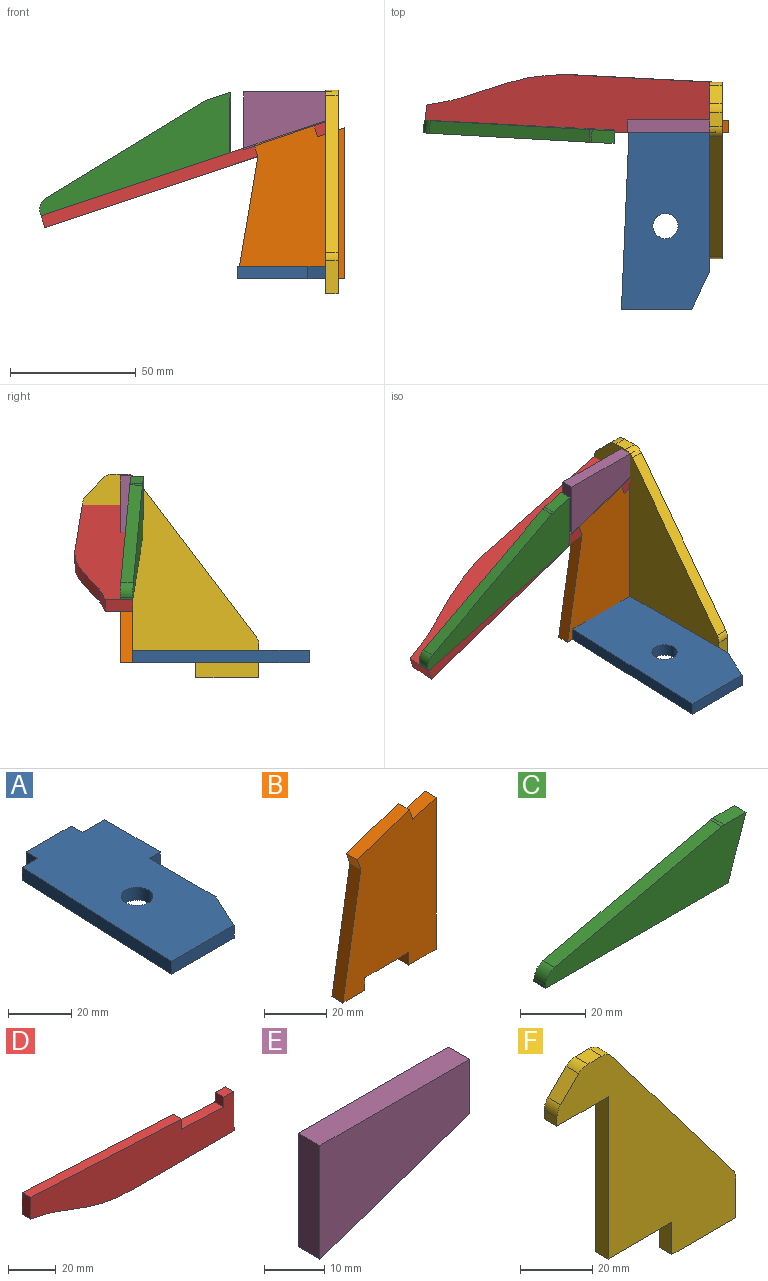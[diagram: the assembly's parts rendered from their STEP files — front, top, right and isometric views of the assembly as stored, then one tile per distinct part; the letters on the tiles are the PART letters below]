
ASSEMBLY  parts=6 mates=5
PART A: 14 faces, bbox 40x75x5 mm
  f0: plane 75x40mm, normal (0,0,1), area 2439mm2, adj f2,f3,f4,f5,f6,f7,f8,f9
  f1: plane 75x40mm, normal (0,0,-1), area 2439mm2, adj f2,f3,f4,f5,f6,f7,f8,f9
  f2: plane 10x5mm, normal (0,1,0), area 50mm2, adj f0,f1,f3,f11
  f3: plane 5x5mm, normal (1,0,0), area 25mm2, adj f0,f1,f2,f4
  f4: plane 20x5mm, normal (0,1,0), area 100mm2, adj f0,f1,f3,f5
  f5: plane 5x5mm, normal (-1,0,0), area 25mm2, adj f0,f1,f4,f6
  f6: plane 7x5mm, normal (0,1,0), area 35mm2, adj f0,f1,f5,f7
  f7: plane 70x5mm, normal (-1,0.04,0), area 350.3mm2, adj f0,f1,f6,f8
  f8: plane 28x5mm, normal (0,-1,0), area 140mm2, adj f0,f1,f7,f13
  f9: plane 30x5mm, normal (1,0,0), area 150mm2, adj f0,f1,f10,f13
  f10: plane 5x5mm, normal (0,-1,0), area 25mm2, adj f0,f1,f9,f11
  f11: plane 25x5mm, normal (1,0,0), area 125mm2, adj f0,f1,f2,f10
  f12: cylinder r=5mm len=10mm, axis (0,0,-1), area 157.1mm2, adj f0,f1
  f13: plane 15x7mm, normal (0.91,-0.42,0), area 82.8mm2, adj f0,f1,f8,f9
PART B: 13 faces, bbox 42.5x5x61.2 mm
  f0: plane 10x5mm, normal (0,0,-1), area 50mm2, adj f1,f10,f11,f12
  f1: plane 5x5mm, normal (1,0,0), area 25mm2, adj f0,f2,f11,f12
  f2: plane 20x5mm, normal (0,0,-1), area 100mm2, adj f1,f3,f11,f12
  f3: plane 5x5mm, normal (-1,0,0), area 25mm2, adj f2,f4,f11,f12
  f4: plane 12.5x5mm, normal (0,0,-1), area 62.5mm2, adj f3,f5,f11,f12
  f5: plane 60x5mm, normal (1,0,0), area 300mm2, adj f4,f6,f11,f12
  f6: plane 10.64x5mm, normal (-0.32,0,0.95), area 56.1mm2, adj f5,f7,f11,f12
  f7: plane 5x4.74mm, normal (0.95,0,0.32), area 25mm2, adj f6,f8,f11,f12
  f8: plane 23.72x7.91mm, normal (-0.32,0,0.95), area 125mm2, adj f7,f9,f11,f12
  f9: plane 5x4.74mm, normal (-0.95,0,-0.32), area 25mm2, adj f8,f10,f11,f12
  f10: plane 48.55x8.14mm, normal (-0.99,0,0.17), area 246.1mm2, adj f0,f9,f11,f12
  f11: plane 61.2x42.5mm, normal (0,-1,0), area 2087.4mm2, adj f0,f1,f2,f3,f4,f5,f6,f7
  f12: plane 61.2x42.5mm, normal (0,1,0), area 2087.4mm2, adj f0,f1,f2,f3,f4,f5,f6,f7
PART C: 9 faces, bbox 86.8x5x22.7 mm
  f0: cylinder r=5mm len=5mm, axis (0,1,0), area 33.6mm2, adj f1,f6,f7,f8
  f1: plane 5x1.02mm, normal (-1,0,0), area 5.1mm2, adj f0,f2,f7,f8
  f2: plane 79x5mm, normal (0,0,-1), area 395mm2, adj f1,f3,f7,f8
  f3: plane 22.69x7.81mm, normal (0.95,0,-0.33), area 120mm2, adj f2,f4,f7,f8
  f4: plane 9.43x5mm, normal (0,0,1), area 47.2mm2, adj f3,f5,f7,f8
  f5: cylinder r=5mm len=5mm, axis (0,1,0), area 5.7mm2, adj f4,f6,f7,f8
  f6: plane 72.38x16.67mm, normal (-0.22,0,0.97), area 371.4mm2, adj f0,f5,f7,f8
  f7: plane 86.81x22.69mm, normal (0,-1,0), area 1198.7mm2, adj f0,f1,f2,f3,f4,f5,f6
  f8: plane 86.81x22.69mm, normal (0,1,0), area 1198.7mm2, adj f0,f1,f2,f3,f4,f5,f6
PART D: 14 faces, bbox 120x5x26 mm
  f0: plane 5.99x5mm, normal (0.05,0,1), area 30mm2, adj f1,f2,f3,f11
  f1: plane 120x26mm, normal (0,-1,0), area 2251.6mm2, adj f0,f3,f4,f5,f6,f7,f8,f9
  f2: plane 120x26mm, normal (0,1,0), area 2251.6mm2, adj f0,f3,f4,f5,f6,f7,f8,f9
  f3: plane 20x5mm, normal (1,0,0), area 100mm2, adj f0,f1,f2,f10
  f4: plane 89.04x5mm, normal (0.05,0,1), area 445.7mm2, adj f1,f2,f5,f12
  f5: plane 11x5mm, normal (-1,0,0), area 55mm2, adj f1,f2,f4,f6
  f6: plane 9.75x5mm, normal (-0.22,0,-0.97), area 50mm2, adj f1,f2,f5,f7
  f7: cylinder r=40mm len=5mm, axis (0,1,0), area 24.4mm2, adj f1,f2,f6,f8
  f8: plane 18.4x6.64mm, normal (-0.34,0,-0.94), area 97.8mm2, adj f1,f2,f7,f9
  f9: cylinder r=80mm len=27.17mm, axis (0,1,0), area 138.6mm2, adj f1,f2,f8,f10
  f10: plane 60x5mm, normal (0,0,-1), area 300mm2, adj f1,f2,f3,f9
  f11: plane 5x4.99mm, normal (-1,0,0.05), area 25mm2, adj f0,f1,f2,f13
  f12: plane 5x4.99mm, normal (1,0,-0.05), area 25mm2, adj f1,f2,f4,f13
  f13: plane 24.97x5mm, normal (0.05,0,1), area 125mm2, adj f1,f2,f11,f12
PART E: 6 faces, bbox 35x5x23 mm
  f0: plane 35x5mm, normal (0,0,1), area 175mm2, adj f1,f3,f4,f5
  f1: plane 23x5mm, normal (-1,0,0), area 115mm2, adj f0,f2,f4,f5
  f2: plane 35x12mm, normal (0.32,0,-0.95), area 185mm2, adj f1,f3,f4,f5
  f3: plane 11x5mm, normal (1,0,0), area 55mm2, adj f0,f2,f4,f5
  f4: plane 35x23mm, normal (0,-1,0), area 595mm2, adj f0,f1,f2,f3
  f5: plane 35x23mm, normal (0,1,0), area 595mm2, adj f0,f1,f2,f3
PART F: 16 faces, bbox 70x5x81 mm
  f0: plane 13.32x5mm, normal (1,0,0), area 66.6mm2, adj f9,f10,f11,f12
  f1: plane 62.68x47.49mm, normal (0.8,0,0.6), area 393.2mm2, adj f10,f11,f12,f13
  f2: plane 5.44x5mm, normal (0,0,1), area 27.2mm2, adj f10,f11,f13,f14
  f3: plane 7.07x7.07mm, normal (-0.71,0,0.71), area 50mm2, adj f10,f11,f14,f15
  f4: plane 5x2.93mm, normal (-1,0,0), area 14.6mm2, adj f5,f10,f11,f15
  f5: plane 20x5mm, normal (0,0,-1), area 100mm2, adj f4,f6,f10,f11
  f6: plane 55x5mm, normal (-1,0,0), area 275mm2, adj f5,f7,f10,f11
  f7: plane 25x5mm, normal (0,0,-1), area 125mm2, adj f6,f8,f10,f11
  f8: plane 11x5mm, normal (-1,0,0), area 55mm2, adj f7,f9,f10,f11
  f9: plane 25x5mm, normal (0,0,-1), area 125mm2, adj f0,f8,f10,f11
  f10: plane 81x70mm, normal (0,-1,0), area 2372.7mm2, adj f0,f1,f2,f3,f4,f5,f6,f7
  f11: plane 81x70mm, normal (0,1,0), area 2372.7mm2, adj f0,f1,f2,f3,f4,f5,f6,f7
  f12: cylinder r=5mm len=5mm, axis (0,1,0), area 16.2mm2, adj f0,f1,f10,f11
  f13: cylinder r=5mm len=5mm, axis (0,1,0), area 23.1mm2, adj f1,f2,f10,f11
  f14: cylinder r=5mm len=5mm, axis (0,1,0), area 19.6mm2, adj f2,f3,f10,f11
  f15: cylinder r=5mm len=5mm, axis (0,1,0), area 19.6mm2, adj f3,f4,f10,f11
PLACE A t=(60.99,-126.96,80.78)mm fixed
PLACE B t=(63.49,-51.96,85.78)mm
PLACE C rot(axis=(0.02,-0.99,-0.15),18.7deg) t=(40.57,-55.92,130.9)mm
PLACE D rot(axis=(0.97,-0.18,0.13),92deg) t=(80.41,-36.99,144.19)mm
PLACE E t=(45.91,-51.96,132.02)mm
PLACE F rot(axis=(0,0,-1),90deg) t=(83.49,-106.96,74.78)mm
MATE fastened F.f8 <-> A.f10  axis (0,1,0) through (80.99,-81.96,85.78)mm
MATE fastened C.f1 <-> D.f5  axis (0.95,-0.05,0.32) through (-34.52,-56.96,105.88)mm
MATE fastened A.f0 <-> B.f2  axis (0,0,1) through (73.49,-51.96,85.78)mm
MATE fastened E.f4 <-> B.f11  axis (0,-1,0) through (63.41,-56.96,138.02)mm
MATE fastened B.f9 <-> D.f12  axis (-0.95,0,-0.32) through (50.84,-54.46,131.7)mm
